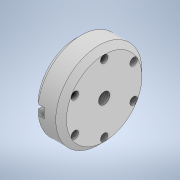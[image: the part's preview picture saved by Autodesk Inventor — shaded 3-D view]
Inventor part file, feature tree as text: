
AUTODESK INVENTOR PART (.ipt)
format: ipt  version: 2022 (Build 260153000, 153)  size: 169,984 bytes
history: native  units: mm
features: sketch x4, revolve x2, other x1, hole x1, extrude x1, thread x1
ambient origin geometry x8: Origin, YZ Plane, XZ Plane, XY Plane, X Axis, Y Axis, Z Axis, Center Point
bodies: Body1 (feature_tree)
feature tree (10):
  other  "Твердое тело1"
  hole  "Отверстие1"  [1 undecoded]
  extrude  "Выдавливание1"  Depth=60.0mm TaperAngle=360.0deg
  thread  "Резьба1"
  sketch  "Эскиз3"
  sketch  "Эскиз4"
  revolve  "Вращение2"
  sketch  "Эскиз1"
  sketch  "Эскиз2"
  revolve  "Вращение1"
note: 1 required parameter value undecoded (feature->parameter linkage not recoverable at this tier; creation-order binding heuristic only, values carry confidence <= 0.55)
